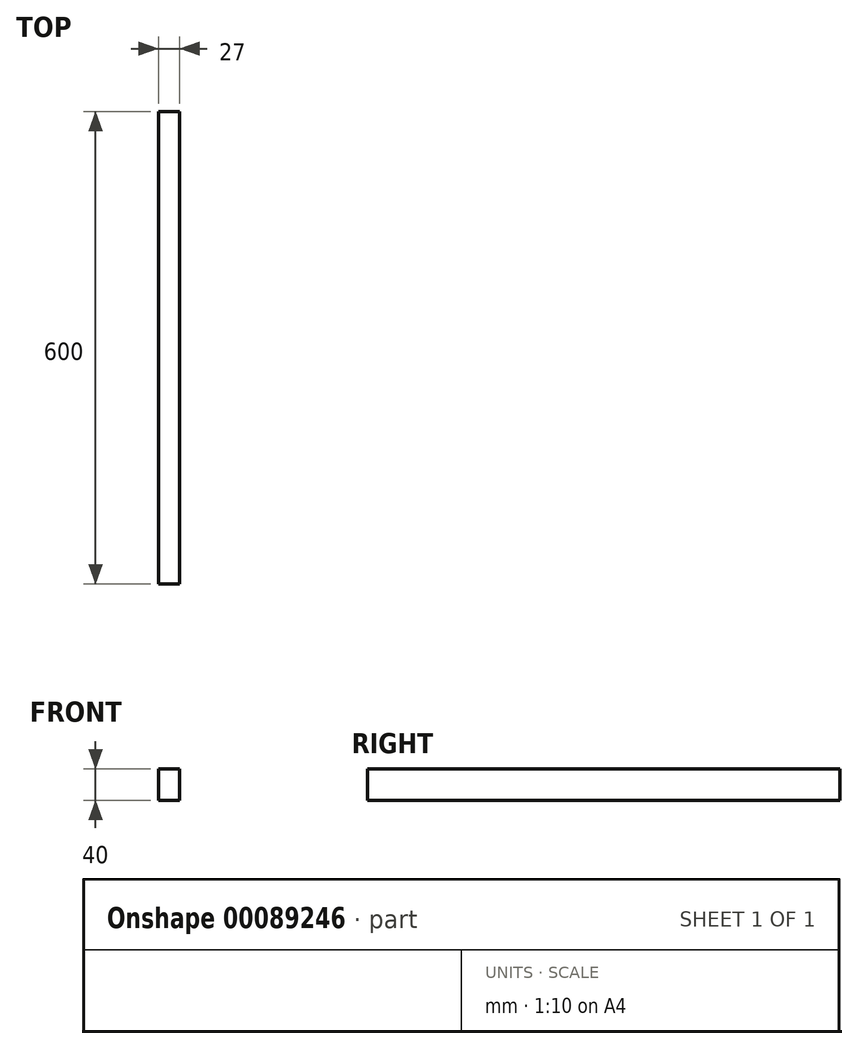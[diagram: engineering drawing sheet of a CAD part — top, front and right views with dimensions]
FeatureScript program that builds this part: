
annotation { "Feature Type Name" : "Feature", "Feature Type Description" : "" }
export const myFeature = defineFeature(function(context is Context, id is Id, definition is map)
    precondition{}
    {
        {
            var Q0;
            Q0=qCreatedBy(makeId("Front.planeOp"),FACE);
            var sketch = newSketch(context, id + "F0", { "sketchPlane" : qUnion([Q0])});
            skLineSegment(sketch, "E0.bottom", {"start": v(-13.5, 20) * mm, "end": v(13.5, 20) * mm});
            skLineSegment(sketch, "E0.top", {"start": v(-13.5, -20) * mm, "end": v(13.5, -20) * mm});
            skLineSegment(sketch, "E0.left", {"start": v(-13.5, 20) * mm, "end": v(-13.5, -20) * mm});
            skLineSegment(sketch, "E0.right", {"start": v(13.5, 20) * mm, "end": v(13.5, -20) * mm});
            skPoint(sketch, "E0.middle", {"position": v(0, 0) * mm});
            skSolve(sketch);
        }
        {
            var Q0;
            Q0=makeQuery(id+"F0.imprint","IMPRINT",FACE,{"disambiguationData":[TD([[makeQuery(id+"F0.imprint","IMPRINT",EDGE,{"derivedFrom":sQuery(id+"F0.wireOp",EDGE,"E0.bottom")}),-1.0]])]});
            extrude(context, id + "F1", {"entities" : qUnion([Q0]), "depth" : 600 * mm});
        }
    });
